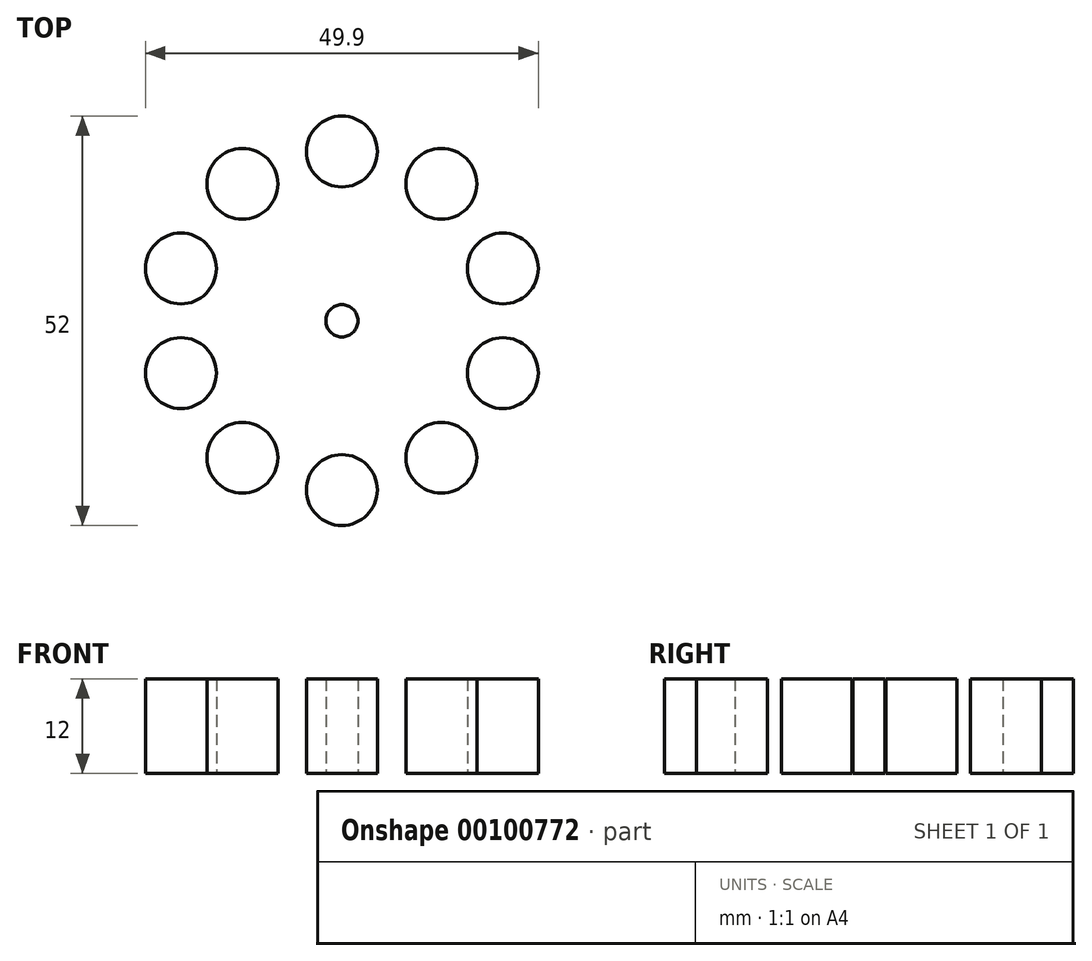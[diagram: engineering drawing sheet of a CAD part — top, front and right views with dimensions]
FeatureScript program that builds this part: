
annotation { "Feature Type Name" : "Feature", "Feature Type Description" : "" }
export const myFeature = defineFeature(function(context is Context, id is Id, definition is map)
    precondition{}
    {
        {
            var Q0;
            Q0=qCreatedBy(makeId("Top.planeOp"),FACE);
            var sketch = newSketch(context, id + "F0", { "sketchPlane" : qUnion([Q0])});
            skCircle(sketch, "E0", {"center": v(0, 0) * mm, "radius": 17 * mm, "construction": true});
            skCircle(sketch, "E1", {"center": v(0, 0) * mm, "radius": 26 * mm, "construction": true});
            skLineSegment(sketch, "E2", {"start": v(0, 17) * mm, "end": v(0, 26) * mm, "construction": true});
            skCircle(sketch, "E3", {"center": v(0, 21.5) * mm, "radius": 4.5 * mm});
            skCircle(sketch, "E4.1.0", {"center": v(-12.64, 17.4) * mm, "radius": 4.5 * mm});
            skCircle(sketch, "E4.2.0", {"center": v(-20.45, 6.64) * mm, "radius": 4.5 * mm});
            skCircle(sketch, "E4.3.0", {"center": v(-20.45, -6.64) * mm, "radius": 4.5 * mm});
            skCircle(sketch, "E4.4.0", {"center": v(-12.64, -17.4) * mm, "radius": 4.5 * mm});
            skCircle(sketch, "E4.5.0", {"center": v(0, -21.5) * mm, "radius": 4.5 * mm});
            skCircle(sketch, "E4.6.0", {"center": v(12.64, -17.4) * mm, "radius": 4.5 * mm});
            skCircle(sketch, "E4.7.0", {"center": v(20.45, -6.64) * mm, "radius": 4.5 * mm});
            skCircle(sketch, "E4.8.0", {"center": v(20.45, 6.64) * mm, "radius": 4.5 * mm});
            skCircle(sketch, "E4.9.0", {"center": v(12.64, 17.4) * mm, "radius": 4.5 * mm});
            skLineSegment(sketch, "E5", {"start": v(0, 0) * mm, "end": v(12.64, 17.4) * mm, "construction": true});
            skLineSegment(sketch, "E6", {"start": v(0, 0) * mm, "end": v(20.45, 6.64) * mm, "construction": true});
            skCircle(sketch, "E7", {"center": v(0, 0) * mm, "radius": 2.04 * mm});
            skSolve(sketch);
        }
        {
            var Q0;
            Q0=makeQuery(id+"F0.imprint","IMPRINT",FACE,{"disambiguationData":[TD([[makeQuery(id+"F0.imprint","IMPRINT",EDGE,{"derivedFrom":sQuery(id+"F0.wireOp",EDGE,"E4.6.0")}),1.0]])]});
            var Q1;
            Q1=makeQuery(id+"F0.imprint","IMPRINT",FACE,{"disambiguationData":[TD([[makeQuery(id+"F0.imprint","IMPRINT",EDGE,{"derivedFrom":sQuery(id+"F0.wireOp",EDGE,"E4.7.0")}),1.0]])]});
            var Q2;
            Q2=makeQuery(id+"F0.imprint","IMPRINT",FACE,{"disambiguationData":[TD([[makeQuery(id+"F0.imprint","IMPRINT",EDGE,{"derivedFrom":sQuery(id+"F0.wireOp",EDGE,"E4.5.0")}),1.0]])]});
            var Q3;
            Q3=makeQuery(id+"F0.imprint","IMPRINT",FACE,{"disambiguationData":[TD([[makeQuery(id+"F0.imprint","IMPRINT",EDGE,{"derivedFrom":sQuery(id+"F0.wireOp",EDGE,"E4.8.0")}),1.0]])]});
            var Q4;
            Q4=makeQuery(id+"F0.imprint","IMPRINT",FACE,{"disambiguationData":[TD([[makeQuery(id+"F0.imprint","IMPRINT",EDGE,{"derivedFrom":sQuery(id+"F0.wireOp",EDGE,"E4.9.0")}),1.0]])]});
            var Q5;
            Q5=makeQuery(id+"F0.imprint","IMPRINT",FACE,{"disambiguationData":[TD([[makeQuery(id+"F0.imprint","IMPRINT",EDGE,{"derivedFrom":sQuery(id+"F0.wireOp",EDGE,"E4.4.0")}),1.0]])]});
            var Q6;
            Q6=makeQuery(id+"F0.imprint","IMPRINT",FACE,{"disambiguationData":[TD([[makeQuery(id+"F0.imprint","IMPRINT",EDGE,{"derivedFrom":sQuery(id+"F0.wireOp",EDGE,"E4.3.0")}),1.0]])]});
            var Q7;
            Q7=makeQuery(id+"F0.imprint","IMPRINT",FACE,{"disambiguationData":[TD([[makeQuery(id+"F0.imprint","IMPRINT",EDGE,{"derivedFrom":sQuery(id+"F0.wireOp",EDGE,"E4.2.0")}),1.0]])]});
            var Q8;
            Q8=makeQuery(id+"F0.imprint","IMPRINT",FACE,{"disambiguationData":[TD([[makeQuery(id+"F0.imprint","IMPRINT",EDGE,{"derivedFrom":sQuery(id+"F0.wireOp",EDGE,"E4.1.0")}),1.0]])]});
            var Q9;
            Q9=makeQuery(id+"F0.imprint","IMPRINT",FACE,{"disambiguationData":[TD([[makeQuery(id+"F0.imprint","IMPRINT",EDGE,{"derivedFrom":sQuery(id+"F0.wireOp",EDGE,"E3")}),1.0]])]});
            var Q10;
            Q10=makeQuery(id+"F0.imprint","IMPRINT",FACE,{"disambiguationData":[TD([[makeQuery(id+"F0.imprint","IMPRINT",EDGE,{"derivedFrom":sQuery(id+"F0.wireOp",EDGE,"E7")}),1.0]])]});
            extrude(context, id + "F1", {"entities" : qUnion([Q0, Q1, Q2, Q3, Q4, Q5, Q6, Q7, Q8, Q9, Q10]), "depth" : 12 * mm});
        }
    });
